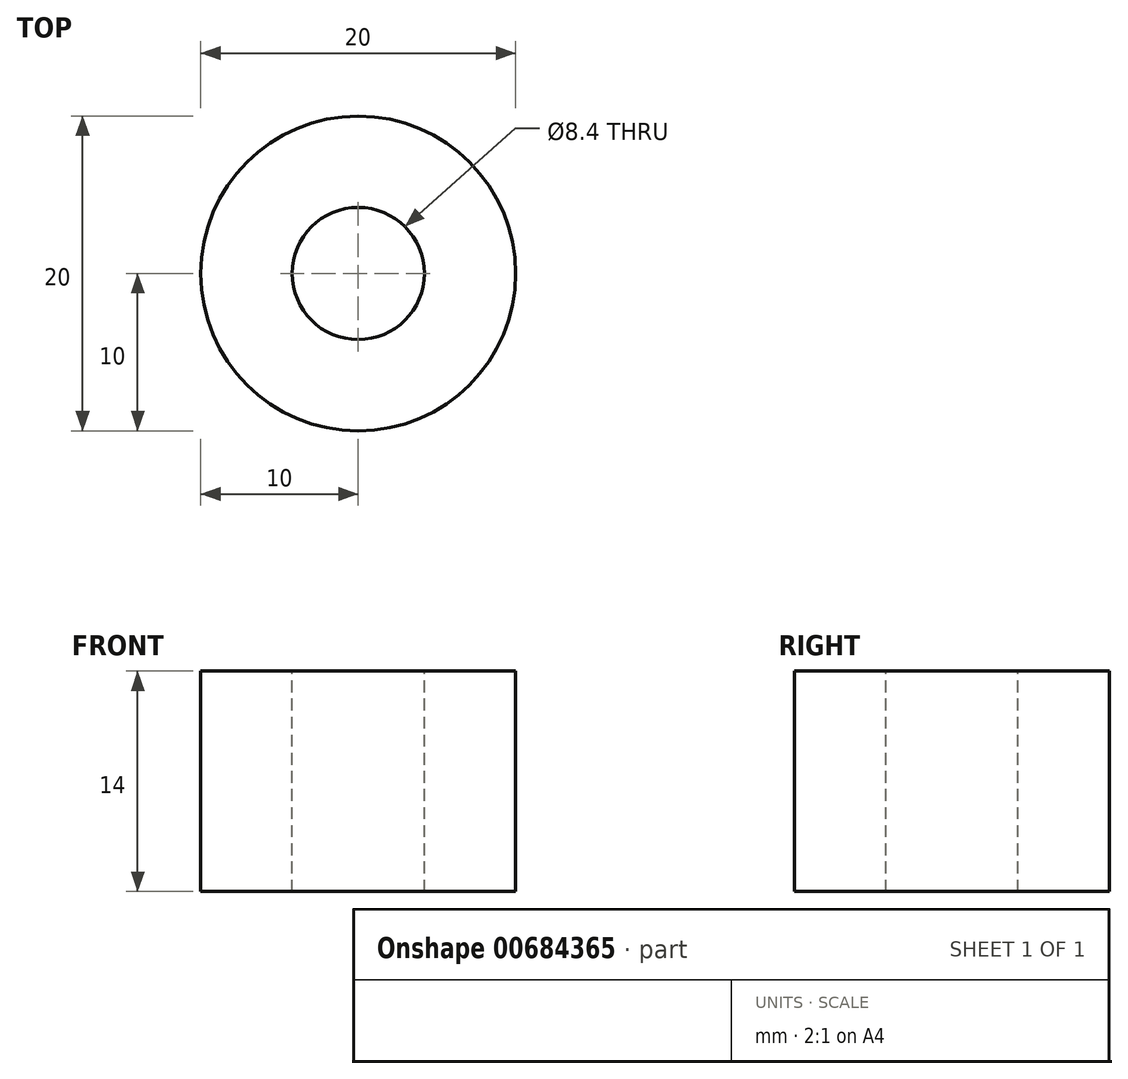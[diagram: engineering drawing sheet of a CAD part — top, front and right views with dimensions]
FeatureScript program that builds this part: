
annotation { "Feature Type Name" : "Feature", "Feature Type Description" : "" }
export const myFeature = defineFeature(function(context is Context, id is Id, definition is map)
    precondition{}
    {
        {
            var Q0;
            Q0=qCreatedBy(makeId("Top.planeOp"),FACE);
            var sketch = newSketch(context, id + "F0", { "sketchPlane" : qUnion([Q0])});
            skCircle(sketch, "E0", {"center": v(0, 0) * mm, "radius": 10 * mm});
            skCircle(sketch, "E1", {"center": v(0, 0) * mm, "radius": 4.2 * mm});
            skSolve(sketch);
        }
        {
            var Q0;
            Q0=makeQuery(id+"F0.imprint","IMPRINT",FACE,{"disambiguationData":[TD([[makeQuery(id+"F0.imprint","IMPRINT",EDGE,{"derivedFrom":sQuery(id+"F0.wireOp",EDGE,"E0")}),1.0]])]});
            extrude(context, id + "F1", {"entities" : qUnion([Q0]), "oppositeDirection" : true, "depth" : 14 * mm, "offsetDistance" : 25 * mm});
        }
    });
